# Revit family: Drain_Floor_9_Inch_Round_Top-Zurn-Z730-Medium-Duty
name_source: partatom
category: Plumbing Fixtures
units: mm (PartAtom-declared; Revit-internal decimal feet)

## family parameters
Always vertical = Yes
Cut with Voids When Loaded = No
Maintain Annotation Orientation = No
OmniClass Number = 23.45.55.21
OmniClass Title = Drains (Wastes)
Part Type = Normal
Room Calculation Point = No
Round Connector Dimension = Use Radius
Shared = No
Work Plane-Based = No

## types (4) — shared parameters
Assembly Code = D2030300
CW Connection = No
Default Elevation = 4 "
Description = 9 [229] TOP MEDIUM-DUTY DRAIN
Dim - H = 7.5 "
Grate Open Area (Sq. In) = 23
HW Connection = No
Main Material = Iron - Zurn - Cast - Painted - Blue
Manufacturer = Zurn Water, LLC
Manufacurer Brand = Zurn
Modified Date = 12/22/2025
Plug Material = Bronze - Zurn - Polished
Product Documentation Link = https://files.zurn.com
Product Installation Sheet URL = https://files.zurn.com
Product Page URL = https://www.zurn.com
Product data url = https://www.bimobject.com
Trap Primer = Yes
URL = www.zurn.com
Vent Connection = No
Waste Connection = Yes
zero-valued in all types: CWFU, HWFU, WFU

## per-type parameters (varying)
| type | A_ Pipe Size (Actual-Inner) | A_ Pipe Size (Actual-Outer Radius) | A_ Pipe Size (Actual-Outer) | A_ Pipe Size (Nominal) | Approx. Weight (Lbs) | Connector Radius | Dim - D | Dim - G | Dim - M | Dim - M (Actual) | Dim - T | E_ Body Height | E_ Body Height (Actual) | Grate Material | Model | NPT Radius | ZN Top | ZN-Top |
| Z730 3 Inch Spigot Outlet | 3.068 " | 1.75 " | 3.5 " | 3 " | 54 " | 1.5 " | 3.125 " | 17.125 " | 4.25 " | 4.25 " | 4 " | 13 " | 13 " | Iron - Zurn - Cast - Painted - Blue | Z730 | 2.25 " | 0 " | No |
| Z730 4 Inch Spigot Outlet | 4.026 " | 2.25 " | 4.5 " | 4 " | 79 " | 2 " | 3.625 " | 19.375 " | 4.75 " | 4.75 " | 5 " | 16 " | 16 " | Iron - Zurn - Cast - Painted - Blue | Z730 | 2.75 " | 0 " | No |
| ZN730 3 Inch Spigot Outlet | 3.068 " | 1.75 " | 3.5 " | 3 " | 54 " | 1.5 " | 3.125 " | 17.125 " | 4.25 " | 4.438 " | 4 " | 13 " | 13.188 " | Bronze - Zurn - Polished Nickel | ZN730 | 2.25 " | 0.188 " | Yes |
| ZN730 4 Inch Spigot Outlet | 4.026 " | 2.25 " | 4.5 " | 4 " | 79 " | 2 " | 3.625 " | 19.375 " | 4.75 " | 4.938 " | 5 " | 16 " | 16.188 " | Bronze - Zurn - Polished Nickel | ZN730 | 2.75 " | 0.188 " | Yes |

## geometry (parser evidence)
native form markers: Blend x2, Sweep x6
no freeform markers — native parametric forms only
